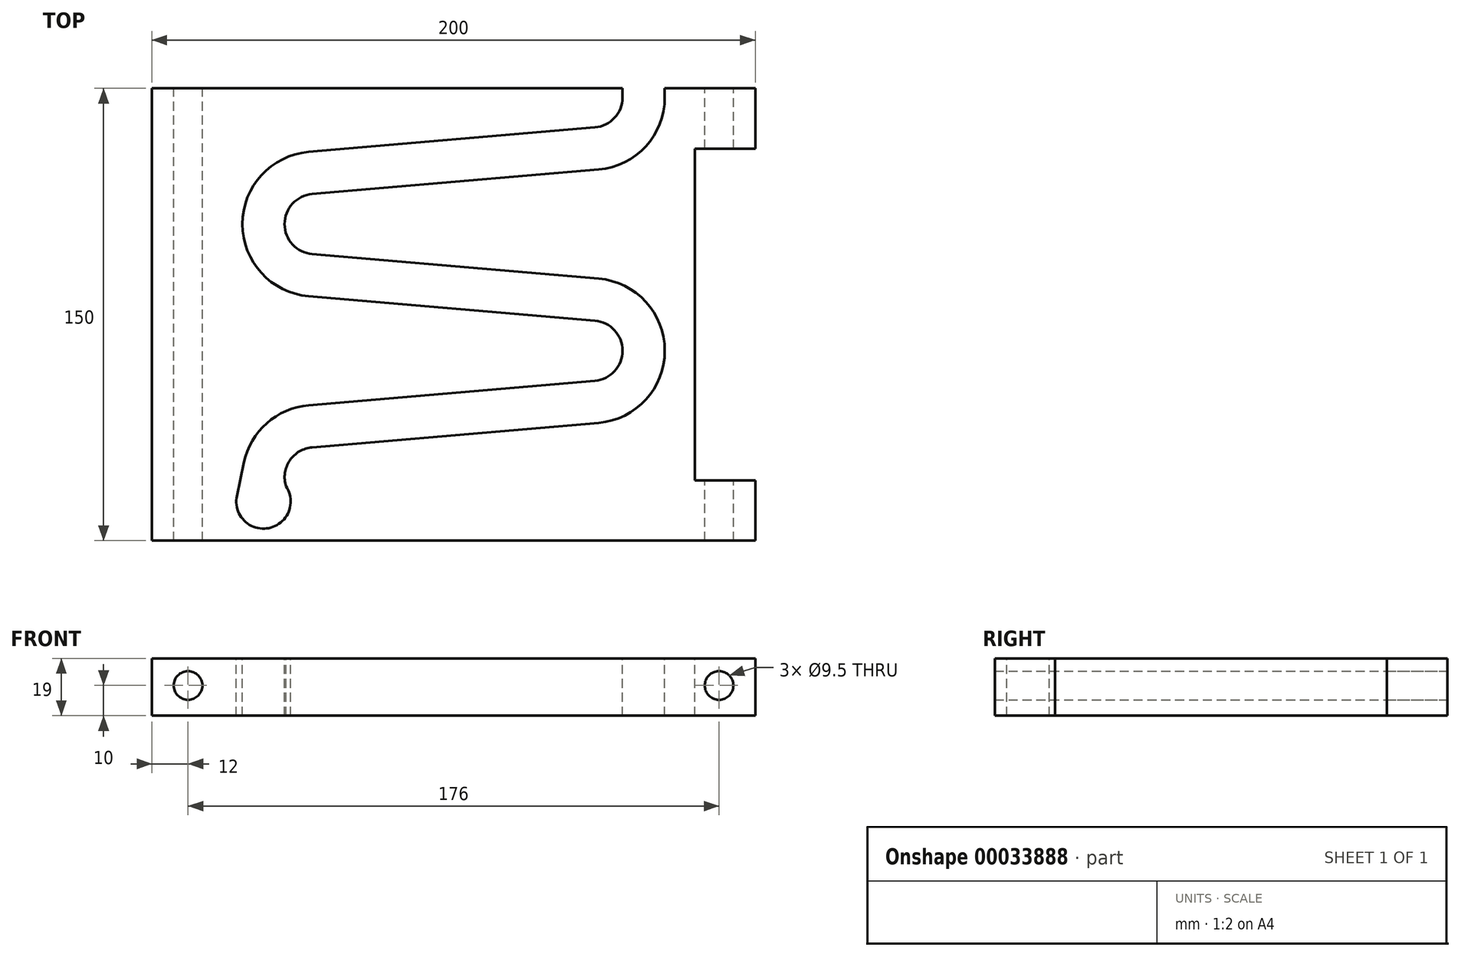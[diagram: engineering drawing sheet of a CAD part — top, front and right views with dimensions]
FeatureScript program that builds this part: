
annotation { "Feature Type Name" : "Feature", "Feature Type Description" : "" }
export const myFeature = defineFeature(function(context is Context, id is Id, definition is map)
    precondition{}
    {
        {
            var Q0;
            Q0=qCreatedBy(makeId("Top.planeOp"),FACE);
            var sketch = newSketch(context, id + "F0", { "sketchPlane" : qUnion([Q0])});
            skLineSegment(sketch, "E0.bottom", {"start": v(0, 0) * mm, "end": v(200, 0) * mm});
            skLineSegment(sketch, "E0.top", {"start": v(0, 150) * mm, "end": v(200, 150) * mm});
            skLineSegment(sketch, "E0.left", {"start": v(0, 0) * mm, "end": v(0, 150) * mm});
            skLineSegment(sketch, "E0.right", {"start": v(200, 0) * mm, "end": v(200, 150) * mm});
            skSolve(sketch);
        }
        {
            var Q0;
            Q0=makeQuery(id+"F0.imprint","IMPRINT",FACE,{"disambiguationData":[TD([[makeQuery(id+"F0.imprint","IMPRINT",EDGE,{"derivedFrom":sQuery(id+"F0.wireOp",EDGE,"E0.bottom")}),1.0]])]});
            extrude(context, id + "F1", {"entities" : qUnion([Q0]), "depth" : 19 * mm});
        }
        {
            var Q0;
            Q0=makeQuery(id+"F1.opExtrude","CAP_FACE",FACE,{"disambiguationData":[OSD([sQuery(id+"F0.wireOp",EDGE,"E0.bottom"),sQuery(id+"F0.wireOp",EDGE,"E0.top"),sQuery(id+"F0.wireOp",EDGE,"E0.left"),sQuery(id+"F0.wireOp",EDGE,"E0.right")])],"isStart":false});
            var sketch = newSketch(context, id + "F2", { "sketchPlane" : qUnion([Q0])});
            skLineSegment(sketch, "E1.0.0", {"start": v(0, 150) * mm, "end": v(0, 0) * mm});
            skLineSegment(sketch, "E1.0.1", {"start": v(0, 0) * mm, "end": v(200, 0) * mm});
            skLineSegment(sketch, "E1.0.2", {"start": v(200, 0) * mm, "end": v(200, 150) * mm});
            skLineSegment(sketch, "E1.0.3", {"start": v(200, 150) * mm, "end": v(0, 150) * mm});
            skLineSegment(sketch, "E2.bottom", {"start": v(0, 150) * mm, "end": v(20, 150) * mm});
            skLineSegment(sketch, "E2.top", {"start": v(0, 130) * mm, "end": v(20, 130) * mm});
            skLineSegment(sketch, "E2.left", {"start": v(0, 150) * mm, "end": v(0, 130) * mm});
            skLineSegment(sketch, "E2.right", {"start": v(20, 150) * mm, "end": v(20, 130) * mm});
            skLineSegment(sketch, "E3.bottom", {"start": v(0, 0) * mm, "end": v(20, 0) * mm});
            skLineSegment(sketch, "E3.top", {"start": v(0, 20) * mm, "end": v(20, 20) * mm});
            skLineSegment(sketch, "E3.left", {"start": v(0, 0) * mm, "end": v(0, 20) * mm});
            skLineSegment(sketch, "E3.right", {"start": v(20, 0) * mm, "end": v(20, 20) * mm});
            skLineSegment(sketch, "E4.bottom", {"start": v(200, 130) * mm, "end": v(180, 130) * mm});
            skLineSegment(sketch, "E4.top", {"start": v(200, 20) * mm, "end": v(180, 20) * mm});
            skLineSegment(sketch, "E4.left", {"start": v(200, 130) * mm, "end": v(200, 20) * mm});
            skLineSegment(sketch, "E4.right", {"start": v(180, 130) * mm, "end": v(180, 20) * mm});
            skSolve(sketch);
        }
        {
            var Q0;
            Q0=makeQuery(id+"F2.imprint","IMPRINT",FACE,{"disambiguationData":[TD([[makeQuery(id+"F2.imprint","IMPRINT",EDGE,{"derivedFrom":sQuery(id+"F2.wireOp",EDGE,"E2.bottom")}),-1.0]])]});
            var Q1;
            Q1=makeQuery(id+"F2.imprint","IMPRINT",FACE,{"disambiguationData":[TD([[makeQuery(id+"F2.imprint","IMPRINT",EDGE,{"derivedFrom":sQuery(id+"F2.wireOp",EDGE,"E3.bottom")}),1.0]])]});
            var Q2;
            Q2=makeQuery(id+"F2.imprint","IMPRINT",FACE,{"disambiguationData":[TD([[makeQuery(id+"F2.imprint","IMPRINT",EDGE,{"derivedFrom":sQuery(id+"F2.wireOp",EDGE,"E4.bottom")}),1.0]])]});
            extrude(context, id + "F3", {"entities" : qUnion([Q0, Q1, Q2]), "operationType" : NewBodyOperationType.REMOVE, "oppositeDirection" : true, "depth" : 19 * mm});
        }
        {
            var Q0;
            Q0=makeQuery(id+"F1.opExtrude","SWEPT_FACE",FACE,{"disambiguationData":[OSD([sQuery(id+"F0.wireOp",EDGE,"E0.top")])]});
            var sketch = newSketch(context, id + "F4", { "sketchPlane" : qUnion([Q0])});
            skCircle(sketch, "E5", {"center": v(-12, 10) * mm, "radius": 4.75 * mm});
            skCircle(sketch, "E6", {"center": v(-188, 10) * mm, "radius": 4.75 * mm});
            skLineSegment(sketch, "E7.0", {"start": v(0, 0) * mm, "end": v(0, 19) * mm});
            skLineSegment(sketch, "E8.0", {"start": v(-200, 19) * mm, "end": v(-200, 0) * mm});
            skSolve(sketch);
        }
        {
            var Q0;
            Q0=makeQuery(id+"F4.imprint","IMPRINT",FACE,{"disambiguationData":[TD([[makeQuery(id+"F4.imprint","IMPRINT",EDGE,{"derivedFrom":sQuery(id+"F4.wireOp",EDGE,"E5")}),1.0]])]});
            var Q1;
            Q1=makeQuery(id+"F4.imprint","IMPRINT",FACE,{"disambiguationData":[TD([[makeQuery(id+"F4.imprint","IMPRINT",EDGE,{"derivedFrom":sQuery(id+"F4.wireOp",EDGE,"E6")}),1.0]])]});
            extrude(context, id + "F5", {"entities" : qUnion([Q0, Q1]), "operationType" : NewBodyOperationType.REMOVE, "oppositeDirection" : true, "depth" : 150 * mm});
        }
        {
            var Q0;
            Q0=makeQuery(id+"F1.opExtrude","CAP_FACE",FACE,{"disambiguationData":[OSD([sQuery(id+"F0.wireOp",EDGE,"E0.bottom"),sQuery(id+"F0.wireOp",EDGE,"E0.top"),sQuery(id+"F0.wireOp",EDGE,"E0.left"),sQuery(id+"F0.wireOp",EDGE,"E0.right")])],"isStart":false});
            var sketch = newSketch(context, id + "F6", { "sketchPlane" : qUnion([Q0])});
            skLineSegment(sketch, "E9", {"start": v(170, 150) * mm, "end": v(170, 147) * mm});
            skLineSegment(sketch, "E10", {"start": v(156, 147) * mm, "end": v(156, 150) * mm});
            skLineSegment(sketch, "E11.0", {"start": v(20, 150) * mm, "end": v(200, 150) * mm});
            skLineSegment(sketch, "E12.0", {"start": v(180, 130) * mm, "end": v(180, 20) * mm});
            skLineSegment(sketch, "E13.0", {"start": v(20, 150) * mm, "end": v(20, 130) * mm});
            skLineSegment(sketch, "E14.0", {"start": v(51.95, 128.91) * mm, "end": v(146.85, 137.04) * mm});
            skArc(sketch, "E15", {"start": v(146.85, 137.04) * mm, "mid": v(153.37, 140.24) * mm, "end": v(156, 147) * mm});
            skArc(sketch, "E16.0", {"start": v(148.05, 123.09) * mm, "mid": v(163.68, 130.77) * mm, "end": v(170, 147) * mm});
            skArc(sketch, "E17", {"start": v(51.95, 128.91) * mm, "mid": v(30, 105) * mm, "end": v(51.95, 81.09) * mm});
            skArc(sketch, "E18", {"start": v(53.15, 114.96) * mm, "mid": v(44, 105) * mm, "end": v(53.15, 95.04) * mm});
            skArc(sketch, "E19", {"start": v(148.05, 39.09) * mm, "mid": v(170, 63) * mm, "end": v(148.05, 86.91) * mm});
            skArc(sketch, "E20", {"start": v(146.85, 53.04) * mm, "mid": v(156, 63) * mm, "end": v(146.85, 72.96) * mm});
            skLineSegment(sketch, "E21", {"start": v(51.95, 81.09) * mm, "end": v(146.85, 72.96) * mm});
            skLineSegment(sketch, "E22", {"start": v(53.15, 95.04) * mm, "end": v(148.05, 86.91) * mm});
            skLineSegment(sketch, "E23.trimOffspring", {"start": v(53.15, 114.96) * mm, "end": v(148.05, 123.09) * mm});
            skArc(sketch, "E24", {"start": v(51.95, 44.91) * mm, "mid": v(38.09, 38.97) * mm, "end": v(30.5, 25.92) * mm});
            skArc(sketch, "E25", {"start": v(53.15, 30.96) * mm, "mid": v(45.71, 26.6) * mm, "end": v(44.44, 18.06) * mm});
            skLineSegment(sketch, "E26", {"start": v(146.85, 53.04) * mm, "end": v(51.95, 44.91) * mm});
            skLineSegment(sketch, "E27", {"start": v(148.05, 39.09) * mm, "end": v(53.15, 30.96) * mm});
            skArc(sketch, "E28", {"start": v(28.2, 14.84) * mm, "mid": v(38.75, 4.17) * mm, "end": v(44.44, 18.06) * mm});
            skPoint(sketch, "E29.orphan", {"position": v(30, 0) * mm});
            skLineSegment(sketch, "E30", {"start": v(30.5, 25.92) * mm, "end": v(28.2, 14.84) * mm});
            skSolve(sketch);
        }
        {
            var Q0;
            {var subQ2=sQuery(id+"F6.wireOp",EDGE,"E9");Q0=makeQuery(id+"F6.imprint","IMPRINT",FACE,{"disambiguationData":[TD([[makeQuery(id+"F6.imprint","IMPRINT",EDGE,{"derivedFrom":subQ2}),-1.0]])]});}
            extrude(context, id + "F7", {"entities" : qUnion([Q0]), "operationType" : NewBodyOperationType.REMOVE, "oppositeDirection" : true, "depth" : 19 * mm});
        }
    });
